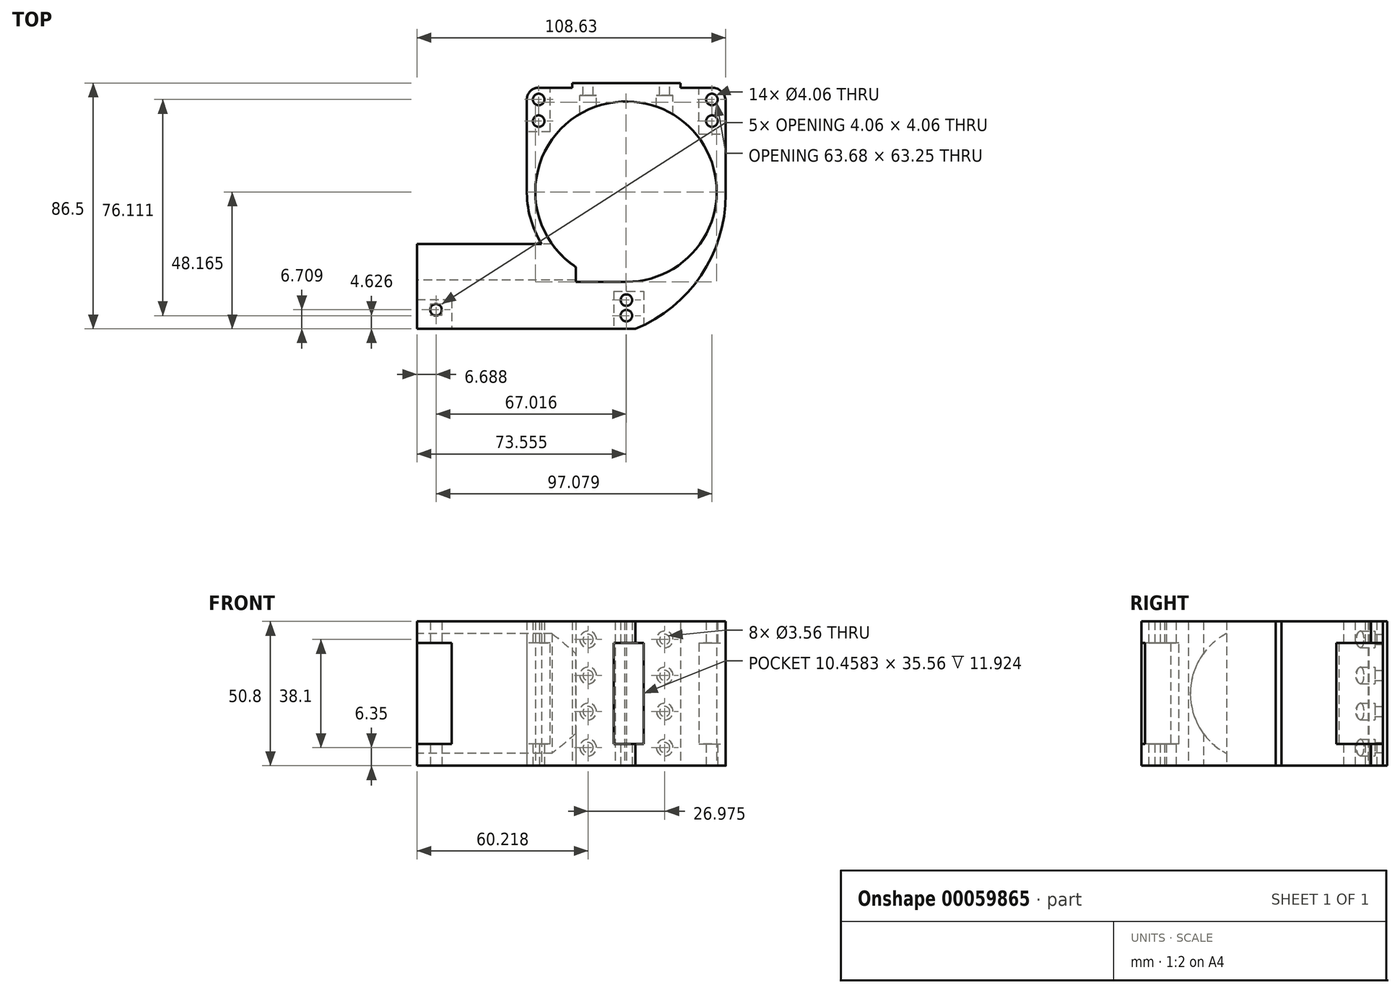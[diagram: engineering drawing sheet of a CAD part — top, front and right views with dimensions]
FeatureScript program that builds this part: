
annotation { "Feature Type Name" : "Feature", "Feature Type Description" : "" }
export const myFeature = defineFeature(function(context is Context, id is Id, definition is map)
    precondition{}
    {
        {
            var Q0;
            Q0=qCreatedBy(makeId("Top.planeOp"),FACE);
            var sketch = newSketch(context, id + "F0", { "sketchPlane" : qUnion([Q0])});
            skArc(sketch, "E0", {"start": v(6.09, -31.72) * mm, "mid": v(37.77, 2.02) * mm, "end": v(2.12, 31.53) * mm});
            skArc(sketch, "E1", {"start": v(9.26, -34.75) * mm, "mid": v(39.57, -9.9) * mm, "end": v(27.72, 27.45) * mm});
            skLineSegment(sketch, "E2", {"start": v(6.09, -31.72) * mm, "end": v(-11.72, -31.72) * mm});
            skLineSegment(sketch, "E3", {"start": v(-11.72, -31.72) * mm, "end": v(-11.72, -26.48) * mm});
            skLineSegment(sketch, "E4", {"start": v(-12.96, 32.48) * mm, "end": v(-12.96, 38.24) * mm});
            skLineSegment(sketch, "E5", {"start": v(-12.96, 38.24) * mm, "end": v(25.14, 38.24) * mm});
            skLineSegment(sketch, "E6", {"start": v(25.14, 38.24) * mm, "end": v(25.14, 32.48) * mm});
            skArc(sketch, "E7", {"start": v(-15.54, 27.45) * mm, "mid": v(-28.39, 6.12) * mm, "end": v(-23.79, -18.36) * mm});
            skArc(sketch, "E8", {"start": v(2.12, 31.53) * mm, "mid": v(-25.12, 7.37) * mm, "end": v(-11.72, -26.48) * mm});
            skPoint(sketch, "E8.third.point", {"position": v(2.12, 31.53) * mm});
            skArc(sketch, "E9.trimOffspring", {"start": v(5.4, -31.72) * mm, "mid": v(5.75, -31.72) * mm, "end": v(6.09, -31.72) * mm});
            skLineSegment(sketch, "E10", {"start": v(-67.62, -18.36) * mm, "end": v(-67.62, -40.45) * mm});
            skLineSegment(sketch, "E11", {"start": v(-15.54, 27.45) * mm, "end": v(-12.96, 32.48) * mm});
            skLineSegment(sketch, "E12", {"start": v(27.72, 27.45) * mm, "end": v(25.14, 32.48) * mm});
            skLineSegment(sketch, "E13", {"start": v(41, -0.96) * mm, "end": v(41, 1.02) * mm});
            skLineSegment(sketch, "E14.bottom", {"start": v(2.91, -34.9) * mm, "end": v(9.26, -34.9) * mm});
            skLineSegment(sketch, "E14.top", {"start": v(2.91, -46.32) * mm, "end": v(9.26, -46.32) * mm});
            skLineSegment(sketch, "E14.left", {"start": v(2.91, -34.9) * mm, "end": v(2.91, -46.32) * mm});
            skLineSegment(sketch, "E14.right", {"start": v(9.26, -34.9) * mm, "end": v(9.26, -46.32) * mm});
            skLineSegment(sketch, "E15", {"start": v(9.26, -34.75) * mm, "end": v(9.26, -34.9) * mm});
            skLineSegment(sketch, "E16", {"start": v(6.08, -46.32) * mm, "end": v(6.08, -34.9) * mm});
            skCircle(sketch, "E17", {"center": v(6.08, -38.14) * mm, "radius": 2.03 * mm});
            skCircle(sketch, "E18", {"center": v(6.08, -43.63) * mm, "radius": 2.03 * mm});
            skLineSegment(sketch, "E19", {"start": v(36.15, 32.48) * mm, "end": v(34.12, 32.48) * mm});
            skPoint(sketch, "E19.endSnap0", {"position": v(-24.79, 31.38) * mm});
            skCircle(sketch, "E20", {"center": v(-24.79, 32.48) * mm, "radius": 2.03 * mm});
            skCircle(sketch, "E21", {"center": v(36.15, 32.48) * mm, "radius": 2.03 * mm});
            skLineSegment(sketch, "E22", {"start": v(-24.79, 32.48) * mm, "end": v(-24.79, 24.86) * mm});
            skLineSegment(sketch, "E23", {"start": v(36.15, 32.48) * mm, "end": v(36.15, 24.86) * mm});
            skCircle(sketch, "E24", {"center": v(-24.79, 24.86) * mm, "radius": 2.03 * mm});
            skCircle(sketch, "E25", {"center": v(36.15, 24.86) * mm, "radius": 2.03 * mm});
            skPoint(sketch, "E26.start.orphan", {"position": v(-28.93, 0.8) * mm});
            skLineSegment(sketch, "E27", {"start": v(-28.93, 0.8) * mm, "end": v(-28.93, 32.48) * mm});
            skPoint(sketch, "E28.start.orphan", {"position": v(-27.99, 38.24) * mm});
            skPoint(sketch, "E29.orphan", {"position": v(41, 38.24) * mm});
            skPoint(sketch, "E30.start.orphan", {"position": v(-24.79, 38.24) * mm});
            skArc(sketch, "E31", {"start": v(-24.51, 36.65) * mm, "mid": v(-27.84, 35.33) * mm, "end": v(-28.93, 31.93) * mm});
            skLineSegment(sketch, "E32", {"start": v(-25.06, 36.65) * mm, "end": v(-12.96, 36.65) * mm});
            skLineSegment(sketch, "E33", {"start": v(41, 1.02) * mm, "end": v(41, 32.48) * mm});
            skPoint(sketch, "E34.end.orphan", {"position": v(36.15, 37.33) * mm});
            skLineSegment(sketch, "E35", {"start": v(-12.96, 36.65) * mm, "end": v(36.15, 36.65) * mm});
            skArc(sketch, "E36", {"start": v(41, 32.48) * mm, "mid": v(39.35, 35.46) * mm, "end": v(36.15, 36.65) * mm});
            skLineSegment(sketch, "E37.trimOffspring", {"start": v(-22.75, 32.48) * mm, "end": v(-24.79, 32.48) * mm});
            skLineSegment(sketch, "E38", {"start": v(2.91, -46.32) * mm, "end": v(-67.62, -46.32) * mm});
            skLineSegment(sketch, "E39", {"start": v(-67.62, -46.32) * mm, "end": v(-67.62, -40.45) * mm});
            skLineSegment(sketch, "E40", {"start": v(-67.62, -18.36) * mm, "end": v(-23.79, -18.36) * mm});
            skCircle(sketch, "E41", {"center": v(-60.93, -41.55) * mm, "radius": 2.03 * mm});
            skLineSegment(sketch, "E42.bottom", {"start": v(-67.62, -46.32) * mm, "end": v(9.26, -46.32) * mm});
            skLineSegment(sketch, "E42.top", {"start": v(-67.62, -48.26) * mm, "end": v(9.26, -48.26) * mm});
            skLineSegment(sketch, "E42.left", {"start": v(-67.62, -46.32) * mm, "end": v(-67.62, -48.26) * mm});
            skLineSegment(sketch, "E42.right", {"start": v(9.26, -46.32) * mm, "end": v(9.26, -48.26) * mm});
            skArc(sketch, "E43", {"start": v(9.26, -48.26) * mm, "mid": v(32.33, -29.44) * mm, "end": v(41, -0.96) * mm});
            skSolve(sketch);
        }
        {
            var Q0;
            Q0 = qSketchRegion(id + "F0", true);
            var Q1;
            {var subQ5=sQuery(id+"F0.wireOp",EDGE,"E14.left");Q1=makeQuery(id+"F0.imprint","IMPRINT",FACE,{"disambiguationData":[TD([[makeQuery(id+"F0.imprint","IMPRINT",EDGE,{"derivedFrom":subQ5}),1.0]])]});}
            var Q2;
            {var subQ6=sQuery(id+"F0.wireOp",EDGE,"E14.right");Q2=makeQuery(id+"F0.imprint","IMPRINT",FACE,{"disambiguationData":[TD([[makeQuery(id+"F0.imprint","IMPRINT",EDGE,{"derivedFrom":subQ6}),-1.0]])]});}
            extrude(context, id + "F1", {"entities" : qUnion([Q0, Q1, Q2]), "depth" : 50.8 * mm});
        }
        {
            var Q0;
            Q0=makeQuery(id+"F1.opExtrude","SWEPT_FACE",FACE,{"disambiguationData":[OSD([sQuery(id+"F0.wireOp",EDGE,"E5")])]});
            var sketch = newSketch(context, id + "F2", { "sketchPlane" : qUnion([Q0])});
            skLineSegment(sketch, "E44", {"start": v(12.96, 25.4) * mm, "end": v(-25.14, 25.4) * mm});
            skPoint(sketch, "E45.orphan", {"position": v(-6.09, 50.8) * mm});
            skLineSegment(sketch, "E46", {"start": v(-6.09, 12.7) * mm, "end": v(-25.14, 12.7) * mm});
            skLineSegment(sketch, "E47", {"start": v(-6.09, 12.7) * mm, "end": v(12.96, 12.7) * mm});
            skLineSegment(sketch, "E48", {"start": v(-6.09, 38.1) * mm, "end": v(-6.09, 50.8) * mm});
            skLineSegment(sketch, "E49", {"start": v(-6.09, 38.1) * mm, "end": v(12.96, 38.1) * mm});
            skLineSegment(sketch, "E50", {"start": v(-6.09, 38.1) * mm, "end": v(-25.14, 38.1) * mm});
            skPoint(sketch, "E51.orphan", {"position": v(-6.09, 0) * mm});
            skPoint(sketch, "E52.orphan", {"position": v(-6.09, 25.4) * mm});
            skLineSegment(sketch, "E53", {"start": v(-6.09, 38.1) * mm, "end": v(-6.09, 25.4) * mm});
            skLineSegment(sketch, "E54", {"start": v(-6.09, 25.4) * mm, "end": v(-6.09, 12.7) * mm});
            skLineSegment(sketch, "E55", {"start": v(-6.09, 12.7) * mm, "end": v(-6.09, 0) * mm});
            skLineSegment(sketch, "E56", {"start": v(-6.09, 6.35) * mm, "end": v(7.39, 6.35) * mm});
            skLineSegment(sketch, "E57", {"start": v(-6.09, 6.35) * mm, "end": v(-19.56, 6.35) * mm});
            skLineSegment(sketch, "E58", {"start": v(-6.09, 19.05) * mm, "end": v(7.39, 19.05) * mm});
            skLineSegment(sketch, "E59", {"start": v(-6.09, 19.05) * mm, "end": v(-19.57, 19.05) * mm});
            skLineSegment(sketch, "E60", {"start": v(-6.09, 31.75) * mm, "end": v(7.4, 31.75) * mm});
            skLineSegment(sketch, "E61", {"start": v(-6.09, 31.75) * mm, "end": v(-19.57, 31.75) * mm});
            skLineSegment(sketch, "E62", {"start": v(-6.09, 44.45) * mm, "end": v(7.4, 44.45) * mm});
            skLineSegment(sketch, "E63", {"start": v(-6.09, 44.45) * mm, "end": v(-19.57, 44.45) * mm});
            skCircle(sketch, "E64", {"center": v(7.39, 6.35) * mm, "radius": 2.92 * mm});
            skCircle(sketch, "E65", {"center": v(7.39, 19.05) * mm, "radius": 2.92 * mm});
            skCircle(sketch, "E66", {"center": v(7.4, 31.75) * mm, "radius": 2.92 * mm});
            skCircle(sketch, "E67", {"center": v(7.4, 44.45) * mm, "radius": 2.92 * mm});
            skCircle(sketch, "E68", {"center": v(-19.56, 6.35) * mm, "radius": 2.92 * mm});
            skCircle(sketch, "E69", {"center": v(-19.57, 19.05) * mm, "radius": 2.92 * mm});
            skCircle(sketch, "E70", {"center": v(-19.57, 31.75) * mm, "radius": 2.92 * mm});
            skCircle(sketch, "E71", {"center": v(-19.57, 44.45) * mm, "radius": 2.92 * mm});
            skSolve(sketch);
        }
        {
            var Q0;
            Q0 = qSketchRegion(id + "F2", true);
            extrude(context, id + "F3", {"entities" : qUnion([Q0]), "operationType" : NewBodyOperationType.REMOVE, "oppositeDirection" : true, "depth" : 25.4 * mm});
        }
        {
            var Q0;
            Q0=makeQuery(id+"F1.opExtrude","SWEPT_FACE",FACE,{"disambiguationData":[OSD([sQuery(id+"F0.wireOp",EDGE,"E5")])]});
            var sketch = newSketch(context, id + "F4", { "sketchPlane" : qUnion([Q0])});
            skCircle(sketch, "E72", {"center": v(7.39, 6.35) * mm, "radius": 1.78 * mm});
            skCircle(sketch, "E73", {"center": v(7.39, 19.05) * mm, "radius": 1.78 * mm});
            skCircle(sketch, "E74", {"center": v(7.4, 31.75) * mm, "radius": 1.78 * mm});
            skCircle(sketch, "E75", {"center": v(7.4, 44.45) * mm, "radius": 1.78 * mm});
            skCircle(sketch, "E76", {"center": v(-19.56, 6.35) * mm, "radius": 1.78 * mm});
            skCircle(sketch, "E77", {"center": v(-19.57, 19.05) * mm, "radius": 1.78 * mm});
            skCircle(sketch, "E78", {"center": v(-19.57, 31.75) * mm, "radius": 1.78 * mm});
            skCircle(sketch, "E79", {"center": v(-19.57, 44.45) * mm, "radius": 1.78 * mm});
            skCircle(sketch, "E80", {"center": v(7.39, 6.35) * mm, "radius": 3.3 * mm});
            skCircle(sketch, "E81", {"center": v(7.39, 19.05) * mm, "radius": 3.34 * mm});
            skCircle(sketch, "E82", {"center": v(7.4, 31.75) * mm, "radius": 3.31 * mm});
            skCircle(sketch, "E83", {"center": v(7.4, 44.45) * mm, "radius": 3.24 * mm});
            skCircle(sketch, "E84", {"center": v(-19.56, 6.35) * mm, "radius": 3.37 * mm});
            skCircle(sketch, "E85", {"center": v(-19.57, 19.05) * mm, "radius": 3.34 * mm});
            skCircle(sketch, "E86", {"center": v(-19.57, 31.75) * mm, "radius": 3.43 * mm});
            skCircle(sketch, "E87", {"center": v(-19.57, 44.45) * mm, "radius": 3.36 * mm});
            skSolve(sketch);
        }
        {
            var Q0;
            Q0 = qSketchRegion(id + "F4", true);
            extrude(context, id + "F5", {"entities" : qUnion([Q0]), "operationType" : NewBodyOperationType.ADD, "oppositeDirection" : true, "depth" : 4.32 * mm});
        }
        {
            var Q0;
            Q0=makeQuery(id+"F1.opExtrude","SWEPT_FACE",FACE,{"disambiguationData":[OSD([sQuery(id+"F0.wireOp",EDGE,"E10")])]});
            var sketch = newSketch(context, id + "F6", { "sketchPlane" : qUnion([Q0])});
            skLineSegment(sketch, "E88", {"start": v(18.36, 25.4) * mm, "end": v(31.06, 25.4) * mm});
            skPoint(sketch, "E88.endSnap0", {"position": v(18.36, 25.4) * mm});
            skLineSegment(sketch, "E89", {"start": v(18.36, 50.8) * mm, "end": v(18.36, 46.48) * mm});
            skLineSegment(sketch, "E90", {"start": v(18.36, 0) * mm, "end": v(18.36, 4.32) * mm});
            skLineSegment(sketch, "E91", {"start": v(18.36, 46.48) * mm, "end": v(18.36, 4.32) * mm});
            skArc(sketch, "E92", {"start": v(18.36, 4.32) * mm, "mid": v(31.06, 25.4) * mm, "end": v(18.36, 46.48) * mm});
            skSolve(sketch);
        }
        {
            var Q0;
            Q0 = qSketchRegion(id + "F6", true);
            extrude(context, id + "F7", {"entities" : qUnion([Q0]), "operationType" : NewBodyOperationType.REMOVE, "oppositeDirection" : true, "depth" : 71 * mm});
        }
        {
            var Q0;
            Q0=makeQuery(id+"F1.opExtrude","SWEPT_FACE",FACE,{"disambiguationData":[OSD([sQuery(id+"F0.wireOp",EDGE,"E27")])]});
            var sketch = newSketch(context, id + "F8", { "sketchPlane" : qUnion([Q0])});
            skLineSegment(sketch, "E93", {"start": v(-31.93, 50.8) * mm, "end": v(-31.93, 43.18) * mm});
            skLineSegment(sketch, "E94", {"start": v(-31.93, 0) * mm, "end": v(-31.93, 7.62) * mm});
            skLineSegment(sketch, "E95.bottom", {"start": v(-31.93, 43.18) * mm, "end": v(-21.14, 43.18) * mm});
            skLineSegment(sketch, "E95.top", {"start": v(-31.93, 7.62) * mm, "end": v(-21.14, 7.62) * mm});
            skLineSegment(sketch, "E95.left", {"start": v(-31.93, 43.18) * mm, "end": v(-31.93, 7.62) * mm});
            skLineSegment(sketch, "E95.right", {"start": v(-21.14, 43.18) * mm, "end": v(-21.14, 7.62) * mm});
            skLineSegment(sketch, "E96.bottom", {"start": v(-31.93, 7.62) * mm, "end": v(-41.89, 7.62) * mm});
            skLineSegment(sketch, "E96.top", {"start": v(-31.93, 43.18) * mm, "end": v(-41.89, 43.18) * mm});
            skLineSegment(sketch, "E96.left", {"start": v(-31.93, 7.62) * mm, "end": v(-31.93, 43.18) * mm});
            skLineSegment(sketch, "E96.right", {"start": v(-41.89, 7.62) * mm, "end": v(-41.89, 43.18) * mm});
            skSolve(sketch);
        }
        {
            var Q0;
            Q0 = qSketchRegion(id + "F8", true);
            extrude(context, id + "F9", {"entities" : qUnion([Q0]), "operationType" : NewBodyOperationType.REMOVE, "oppositeDirection" : true, "depth" : 8.16 * mm});
        }
        {
            var Q0;
            Q0=makeQuery(id+"F1.opExtrude","SWEPT_FACE",FACE,{"disambiguationData":[OSD([sQuery(id+"F0.wireOp",EDGE,"E27")])]});
            var sketch = newSketch(context, id + "F10", { "sketchPlane" : qUnion([Q0])});
            skLineSegment(sketch, "E97.bottom", {"start": v(-30.66, 7.62) * mm, "end": v(-44.86, 7.62) * mm});
            skLineSegment(sketch, "E97.top", {"start": v(-30.66, 43.18) * mm, "end": v(-44.86, 43.18) * mm});
            skLineSegment(sketch, "E97.left", {"start": v(-30.66, 7.62) * mm, "end": v(-30.66, 43.18) * mm});
            skLineSegment(sketch, "E97.right", {"start": v(-44.86, 7.62) * mm, "end": v(-44.86, 43.18) * mm});
            skSolve(sketch);
        }
        {
            var Q0;
            Q0 = qSketchRegion(id + "F10", true);
            extrude(context, id + "F11", {"entities" : qUnion([Q0]), "operationType" : NewBodyOperationType.REMOVE, "depth" : 25.4 * mm});
        }
        {
            var Q0;
            Q0=makeQuery(id+"F1.opExtrude","SWEPT_FACE",FACE,{"disambiguationData":[OSD([sQuery(id+"F0.wireOp",EDGE,"E33")])]});
            var sketch = newSketch(context, id + "F12", { "sketchPlane" : qUnion([Q0])});
            skLineSegment(sketch, "E98", {"start": v(32.48, 50.8) * mm, "end": v(32.48, 43.18) * mm});
            skLineSegment(sketch, "E99", {"start": v(32.48, 0) * mm, "end": v(32.48, 7.62) * mm});
            skLineSegment(sketch, "E100.bottom", {"start": v(32.48, 43.18) * mm, "end": v(41.86, 43.18) * mm});
            skLineSegment(sketch, "E100.top", {"start": v(32.48, 7.62) * mm, "end": v(41.86, 7.62) * mm});
            skLineSegment(sketch, "E100.left", {"start": v(32.48, 43.18) * mm, "end": v(32.48, 7.62) * mm});
            skLineSegment(sketch, "E100.right", {"start": v(41.86, 43.18) * mm, "end": v(41.86, 7.62) * mm});
            skLineSegment(sketch, "E101.bottom", {"start": v(41.86, 7.62) * mm, "end": v(20.33, 7.62) * mm});
            skLineSegment(sketch, "E101.top", {"start": v(41.86, 43.18) * mm, "end": v(20.33, 43.18) * mm});
            skLineSegment(sketch, "E101.left", {"start": v(41.86, 7.62) * mm, "end": v(41.86, 43.18) * mm});
            skLineSegment(sketch, "E101.right", {"start": v(20.33, 7.62) * mm, "end": v(20.33, 43.18) * mm});
            skSolve(sketch);
        }
        {
            var Q0;
            Q0 = qSketchRegion(id + "F12", true);
            extrude(context, id + "F13", {"entities" : qUnion([Q0]), "operationType" : NewBodyOperationType.REMOVE, "oppositeDirection" : true, "depth" : 9.47 * mm});
        }
        {
            var Q0;
            Q0=makeQuery(id+"F1.opExtrude","SWEPT_FACE",FACE,{"disambiguationData":[OSD([sQuery(id+"F0.wireOp",EDGE,"E42.top")])]});
            var sketch = newSketch(context, id + "F14", { "sketchPlane" : qUnion([Q0])});
            skLineSegment(sketch, "E102.bottom", {"start": v(-67.62, 0) * mm, "end": v(-55.36, 0) * mm});
            skLineSegment(sketch, "E102.top", {"start": v(-67.62, 50.8) * mm, "end": v(-55.36, 50.8) * mm});
            skLineSegment(sketch, "E102.left", {"start": v(-67.62, 0) * mm, "end": v(-67.62, 50.8) * mm});
            skLineSegment(sketch, "E102.right", {"start": v(-55.36, 0) * mm, "end": v(-55.36, 50.8) * mm});
            skLineSegment(sketch, "E103", {"start": v(-61.5, 0) * mm, "end": v(-61.5, 7.62) * mm});
            skLineSegment(sketch, "E104", {"start": v(-61.5, 50.8) * mm, "end": v(-61.5, 43.18) * mm});
            skLineSegment(sketch, "E105", {"start": v(-67.62, 43.18) * mm, "end": v(-55.36, 43.18) * mm});
            skLineSegment(sketch, "E106", {"start": v(-67.62, 7.62) * mm, "end": v(-55.36, 7.62) * mm});
            skSolve(sketch);
        }
        {
            var Q0;
            {var subQ0=sQuery(id+"F14.wireOp",EDGE,"E105");var subQ4=sQuery(id+"F14.wireOp",EDGE,"E102.left");var subQ5=makeQuery(id+"F14.imprint","INTERSECT",VERTEX,{"derivedFrom":[subQ4,subQ0]});Q0=makeQuery(id+"F14.imprint","IMPRINT",FACE,{"disambiguationData":[TD([[makeQuery(id+"F14.imprint","IMPRINT",EDGE,{"disambiguationData":[TD([[subQ5,-1.0]])],"derivedFrom":subQ4}),1.0]])]});}
            extrude(context, id + "F15", {"entities" : qUnion([Q0]), "operationType" : NewBodyOperationType.REMOVE, "oppositeDirection" : true, "depth" : 10.27 * mm});
        }
        {
            var Q0;
            Q0=makeQuery(id+"F1.opExtrude","SWEPT_FACE",FACE,{"disambiguationData":[OSD([sQuery(id+"F0.wireOp",EDGE,"E42.top")])]});
            var sketch = newSketch(context, id + "F16", { "sketchPlane" : qUnion([Q0])});
            skLineSegment(sketch, "E107", {"start": v(9.26, 0) * mm, "end": v(9.26, 7.62) * mm});
            skLineSegment(sketch, "E108", {"start": v(9.26, 50.8) * mm, "end": v(9.26, 43.18) * mm});
            skLineSegment(sketch, "E109.bottom", {"start": v(9.26, 7.62) * mm, "end": v(1.64, 7.62) * mm});
            skLineSegment(sketch, "E109.top", {"start": v(9.26, 43.18) * mm, "end": v(1.64, 43.18) * mm});
            skLineSegment(sketch, "E109.left", {"start": v(9.26, 7.62) * mm, "end": v(9.26, 43.18) * mm});
            skLineSegment(sketch, "E109.right", {"start": v(1.64, 7.62) * mm, "end": v(1.64, 43.18) * mm});
            skLineSegment(sketch, "E110.bottom", {"start": v(9.26, 7.62) * mm, "end": v(12.1, 7.62) * mm});
            skLineSegment(sketch, "E110.top", {"start": v(9.26, 43.18) * mm, "end": v(12.1, 43.18) * mm});
            skLineSegment(sketch, "E110.right", {"start": v(12.1, 7.62) * mm, "end": v(12.1, 43.18) * mm});
            skSolve(sketch);
        }
        {
            var Q0;
            Q0 = qSketchRegion(id + "F16", true);
            extrude(context, id + "F17", {"entities" : qUnion([Q0]), "operationType" : NewBodyOperationType.REMOVE, "oppositeDirection" : true, "depth" : 13.2 * mm});
        }
    });
